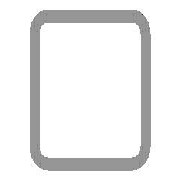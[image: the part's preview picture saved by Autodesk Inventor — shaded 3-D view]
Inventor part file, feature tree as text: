
AUTODESK INVENTOR PART (.ipt)
format: ipt  version: 2022 (Build 260153000, 153)  size: 266,240 bytes
history: native  units: mm (DEFAULTED — no unit token found)
features: other x7, sketch x3, surface_op x2, plane x1
ambient origin geometry x8: Origin, YZ Plane, XZ Plane, XY Plane, X Axis, Y Axis, Z Axis, Center Point
bodies: Body (feature_tree), Solid7 (feature_tree)
feature tree (13):
  parser-record x1  (decoder bookkeeping rows leaked as tree rows — omitted from the tree; the rows remain in map.json)
  other  "Driven Length"
  other  "Start Plane"
  other  "End Plane"
  sketch  "Sketch"  dims[d7=8.0mm d9=40.0mm d11=40.0mm d12=4.0mm d13=-0.0mm d14=180.0mm d15=20.0mm d16=20.0mm d17=90.0deg d18=180.0mm d109=5.0mm d110=5.0mm d111=5.0mm d112=5.0mm d113=5.0mm d114=5.0mm d115=5.0mm d116=5.0mm d117=0.0mm d118=5.0mm d119=5.0mm d120=5.0mm d121=5.0mm d122=5.0mm d123=5.0mm d124=5.0mm d125=5.0mm d126=0.0mm]
  sketch  "Sketch3"  dims[d3=155.0mm]
  plane  "Work Plane3"
  sketch  "Sketch4"  dims[d4=0.0mm]
  other  "Srf17"
  other  "Srf18"
  other  "Srf16"
  surface_op  "Boundary Patch11"
  surface_op  "Boundary Patch12"
